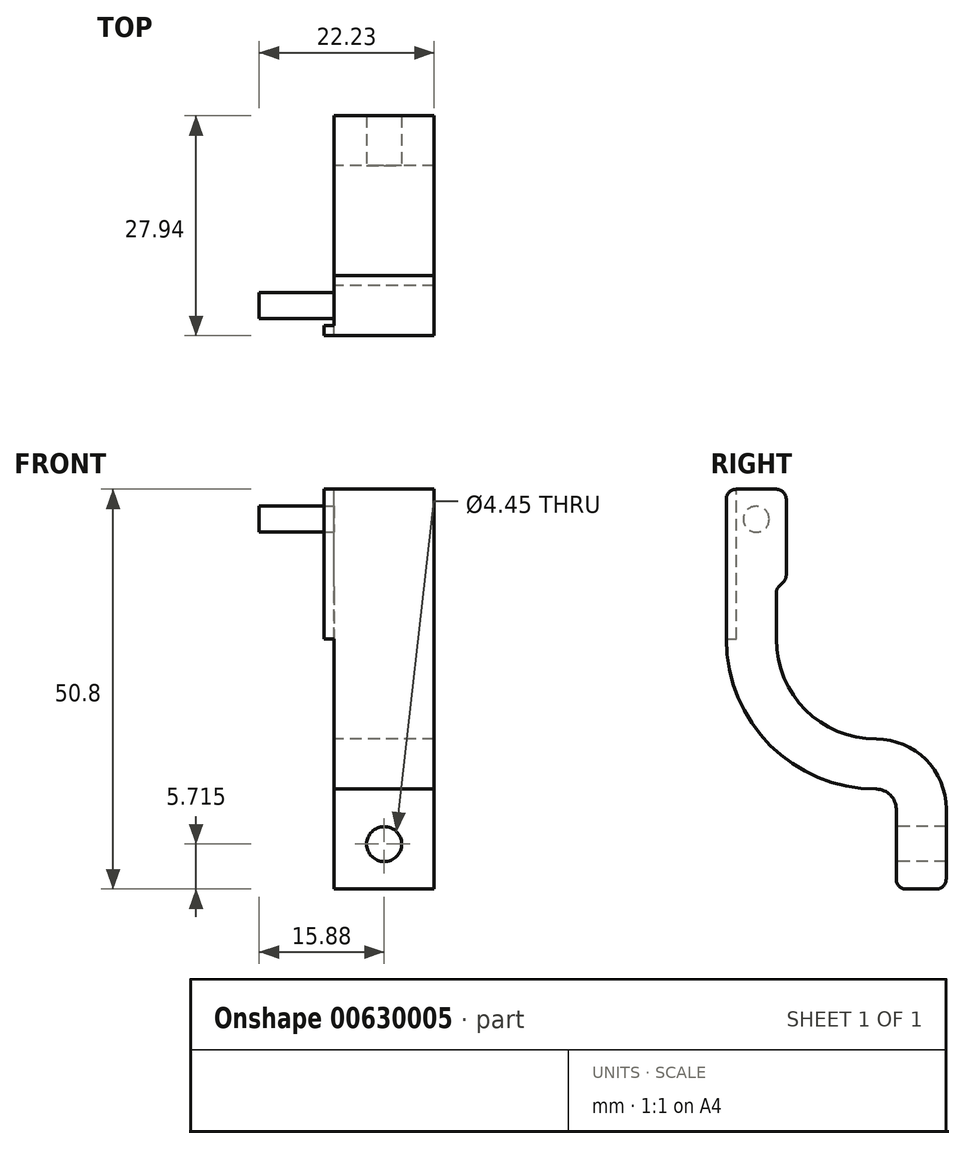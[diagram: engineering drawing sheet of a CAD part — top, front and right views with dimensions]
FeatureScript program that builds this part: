
annotation { "Feature Type Name" : "Feature", "Feature Type Description" : "" }
export const myFeature = defineFeature(function(context is Context, id is Id, definition is map)
    precondition{}
    {
        {
            var Q0;
            Q0=qCreatedBy(makeId("Right.planeOp"),FACE);
            var sketch = newSketch(context, id + "F0", { "sketchPlane" : qUnion([Q0])});
            skLineSegment(sketch, "E0", {"start": v(-25.4, 0) * mm, "end": v(25.4, 0) * mm});
            skArc(sketch, "E1", {"start": v(-25.4, 0) * mm, "mid": v(0, -17.19) * mm, "end": v(25.4, 0) * mm});
            skCircle(sketch, "E2", {"center": v(-22.05, 2.54) * mm, "radius": 0.4 * mm});
            skCircle(sketch, "E3.1.0.0", {"center": v(-13.4, 2.54) * mm, "radius": 0.4 * mm});
            skCircle(sketch, "E3.2.0.0", {"center": v(-4.77, 2.54) * mm, "radius": 0.4 * mm});
            skCircle(sketch, "E3.3.0.0", {"center": v(3.86, 2.54) * mm, "radius": 0.4 * mm});
            skCircle(sketch, "E3.4.0.0", {"center": v(12.5, 2.54) * mm, "radius": 0.4 * mm});
            skCircle(sketch, "E3.5.0.0", {"center": v(21.13, 2.54) * mm, "radius": 0.4 * mm});
            skLineSegment(sketch, "E3.direction1", {"start": v(-22.05, 2.54) * mm, "end": v(-13.4, 2.54) * mm, "construction": true});
            skSolve(sketch);
        }
        {
            var Q0;
            Q0=qCreatedBy(makeId("Right.planeOp"),FACE);
            var sketch = newSketch(context, id + "F1", { "sketchPlane" : qUnion([Q0])});
            skLineSegment(sketch, "E4", {"start": v(-26.67, 0) * mm, "end": v(-26.67, -19.05) * mm});
            skLineSegment(sketch, "E5", {"start": v(-26.67, -19.05) * mm, "end": v(-5.08, -19.05) * mm});
            skLineSegment(sketch, "E6", {"start": v(-5.08, -19.05) * mm, "end": v(-5.08, -38.1) * mm});
            skLineSegment(sketch, "E7.0", {"start": v(-11.43, -25.4) * mm, "end": v(-11.43, -38.1) * mm});
            skLineSegment(sketch, "E7.1", {"start": v(-33.02, -25.4) * mm, "end": v(-11.43, -25.4) * mm});
            skLineSegment(sketch, "E7.2", {"start": v(-33.02, 12.7) * mm, "end": v(-33.02, -25.4) * mm});
            skLineSegment(sketch, "E8", {"start": v(-11.43, -38.1) * mm, "end": v(-5.08, -38.1) * mm});
            skLineSegment(sketch, "E9", {"start": v(-26.67, 0) * mm, "end": v(-25.4, 1.27) * mm});
            skLineSegment(sketch, "E10", {"start": v(-25.4, 1.27) * mm, "end": v(-25.4, 12.7) * mm});
            skLineSegment(sketch, "E11", {"start": v(-25.4, 12.7) * mm, "end": v(-33.02, 12.7) * mm});
            skSolve(sketch);
        }
        {
            var Q0;
            Q0 = qSketchRegion(id + "F1", true);
            extrude(context, id + "F2", {"entities" : qUnion([Q0]), "depth" : 12.7 * mm, "offsetDistance" : 25.4 * mm});
        }
        {
            var Q0;
            Q0=makeQuery(id+"F2.opExtrude","SWEPT_EDGE",EDGE,{"disambiguationData":[OSD([sQuery(id+"F1.wireOp",EDGE,"E4"),sQuery(id+"F1.wireOp",EDGE,"E5")])]});
            fillet(context, id + "F3", {"entities" : qUnion([Q0]), "radius" : 12.7 * mm, "tangentPropagation" : true, "allowEdgeOverflow" : false});
        }
        {
            var Q0;
            Q0=makeQuery(id+"F2.opExtrude","SWEPT_EDGE",EDGE,{"disambiguationData":[OSD([sQuery(id+"F1.wireOp",EDGE,"E7.1"),sQuery(id+"F1.wireOp",EDGE,"E7.2")])]});
            fillet(context, id + "F4", {"entities" : qUnion([Q0]), "radius" : 19.05 * mm, "tangentPropagation" : true, "allowEdgeOverflow" : false});
        }
        {
            var Q0;
            Q0=makeQuery(id+"F2.opExtrude","SWEPT_EDGE",EDGE,{"disambiguationData":[OSD([sQuery(id+"F1.wireOp",EDGE,"E5"),sQuery(id+"F1.wireOp",EDGE,"E6")])]});
            fillet(context, id + "F5", {"entities" : qUnion([Q0]), "radius" : 8.9 * mm, "tangentPropagation" : true, "allowEdgeOverflow" : false});
        }
        {
            var Q0;
            Q0=makeQuery(id+"F2.opExtrude","SWEPT_EDGE",EDGE,{"disambiguationData":[OSD([sQuery(id+"F1.wireOp",EDGE,"E7.0"),sQuery(id+"F1.wireOp",EDGE,"E7.1")])]});
            fillet(context, id + "F6", {"entities" : qUnion([Q0]), "radius" : 2.54 * mm, "tangentPropagation" : true, "allowEdgeOverflow" : false});
        }
        {
            var Q0;
            Q0=makeQuery(id+"F2.opExtrude","SWEPT_EDGE",EDGE,{"disambiguationData":[OSD([sQuery(id+"F1.wireOp",EDGE,"E4"),sQuery(id+"F1.wireOp",EDGE,"E9")])]});
            var Q1;
            Q1=makeQuery(id+"F2.opExtrude","SWEPT_EDGE",EDGE,{"disambiguationData":[OSD([sQuery(id+"F1.wireOp",EDGE,"E9"),sQuery(id+"F1.wireOp",EDGE,"E10")])]});
            var Q2;
            Q2=makeQuery(id+"F2.opExtrude","SWEPT_EDGE",EDGE,{"disambiguationData":[OSD([sQuery(id+"F1.wireOp",EDGE,"E10"),sQuery(id+"F1.wireOp",EDGE,"E11")])]});
            var Q3;
            Q3=makeQuery(id+"F2.opExtrude","SWEPT_EDGE",EDGE,{"disambiguationData":[OSD([sQuery(id+"F1.wireOp",EDGE,"E7.2"),sQuery(id+"F1.wireOp",EDGE,"E11")])]});
            var Q4;
            Q4=makeQuery(id+"F2.opExtrude","SWEPT_EDGE",EDGE,{"disambiguationData":[OSD([sQuery(id+"F1.wireOp",EDGE,"E7.0"),sQuery(id+"F1.wireOp",EDGE,"E8")])]});
            var Q5;
            Q5=makeQuery(id+"F2.opExtrude","SWEPT_EDGE",EDGE,{"disambiguationData":[OSD([sQuery(id+"F1.wireOp",EDGE,"E6"),sQuery(id+"F1.wireOp",EDGE,"E8")])]});
            fillet(context, id + "F7", {"entities" : qUnion([Q0, Q1, Q2, Q3, Q4, Q5]), "radius" : 1.27 * mm, "tangentPropagation" : true, "allowEdgeOverflow" : false});
        }
        {
            var Q0;
            Q0=makeQuery(id+"F2.opExtrude","SWEPT_FACE",FACE,{"disambiguationData":[OSD([sQuery(id+"F1.wireOp",EDGE,"E7.0")])]});
            var sketch = newSketch(context, id + "F8", { "sketchPlane" : qUnion([Q0])});
            skCircle(sketch, "E12", {"center": v(6.35, -32.39) * mm, "radius": 2.22 * mm});
            skSolve(sketch);
        }
        {
            var Q0;
            Q0 = qSketchRegion(id + "F8", true);
            extrude(context, id + "F9", {"entities" : qUnion([Q0]), "operationType" : NewBodyOperationType.REMOVE, "oppositeDirection" : true, "depth" : 6.35 * mm, "offsetDistance" : 25.4 * mm});
        }
        {
            var Q0;
            Q0=makeQuery(id+"F2.opExtrude","CAP_FACE",FACE,{"disambiguationData":[OSD([sQuery(id+"F1.wireOp",EDGE,"E4"),sQuery(id+"F1.wireOp",EDGE,"E5"),sQuery(id+"F1.wireOp",EDGE,"E6"),sQuery(id+"F1.wireOp",EDGE,"E7.0"),sQuery(id+"F1.wireOp",EDGE,"E7.1"),sQuery(id+"F1.wireOp",EDGE,"E7.2"),sQuery(id+"F1.wireOp",EDGE,"E8"),sQuery(id+"F1.wireOp",EDGE,"E9"),sQuery(id+"F1.wireOp",EDGE,"E10"),sQuery(id+"F1.wireOp",EDGE,"E11")])],"isStart":true});
            var sketch = newSketch(context, id + "F10", { "sketchPlane" : qUnion([Q0])});
            skCircle(sketch, "E13", {"center": v(29.21, 8.9) * mm, "radius": 1.65 * mm});
            skSolve(sketch);
        }
        {
            var Q0;
            Q0 = qSketchRegion(id + "F10", true);
            extrude(context, id + "F11", {"entities" : qUnion([Q0]), "operationType" : NewBodyOperationType.ADD, "depth" : 9.52 * mm, "offsetDistance" : 25.4 * mm});
        }
        {
            var Q0;
            Q0=makeQuery(id+"F2.opExtrude","CAP_FACE",FACE,{"disambiguationData":[OSD([sQuery(id+"F1.wireOp",EDGE,"E4"),sQuery(id+"F1.wireOp",EDGE,"E5"),sQuery(id+"F1.wireOp",EDGE,"E6"),sQuery(id+"F1.wireOp",EDGE,"E7.0"),sQuery(id+"F1.wireOp",EDGE,"E7.1"),sQuery(id+"F1.wireOp",EDGE,"E7.2"),sQuery(id+"F1.wireOp",EDGE,"E8"),sQuery(id+"F1.wireOp",EDGE,"E9"),sQuery(id+"F1.wireOp",EDGE,"E10"),sQuery(id+"F1.wireOp",EDGE,"E11")])],"isStart":true});
            var sketch = newSketch(context, id + "F12", { "sketchPlane" : qUnion([Q0])});
            skLineSegment(sketch, "E14.bottom", {"start": v(33.02, -6.35) * mm, "end": v(31.75, -6.35) * mm});
            skLineSegment(sketch, "E14.left", {"start": v(33.02, -6.35) * mm, "end": v(33.02, 11.43) * mm});
            skLineSegment(sketch, "E14.right", {"start": v(31.75, -6.35) * mm, "end": v(31.75, 12.7) * mm});
            skArc(sketch, "E15", {"start": v(33.02, 11.43) * mm, "mid": v(32.65, 12.33) * mm, "end": v(31.75, 12.7) * mm});
            skSolve(sketch);
        }
        {
            var Q0;
            Q0 = qSketchRegion(id + "F12", true);
            extrude(context, id + "F13", {"entities" : qUnion([Q0]), "operationType" : NewBodyOperationType.ADD, "depth" : 1.27 * mm, "offsetDistance" : 25.4 * mm});
        }
    });
